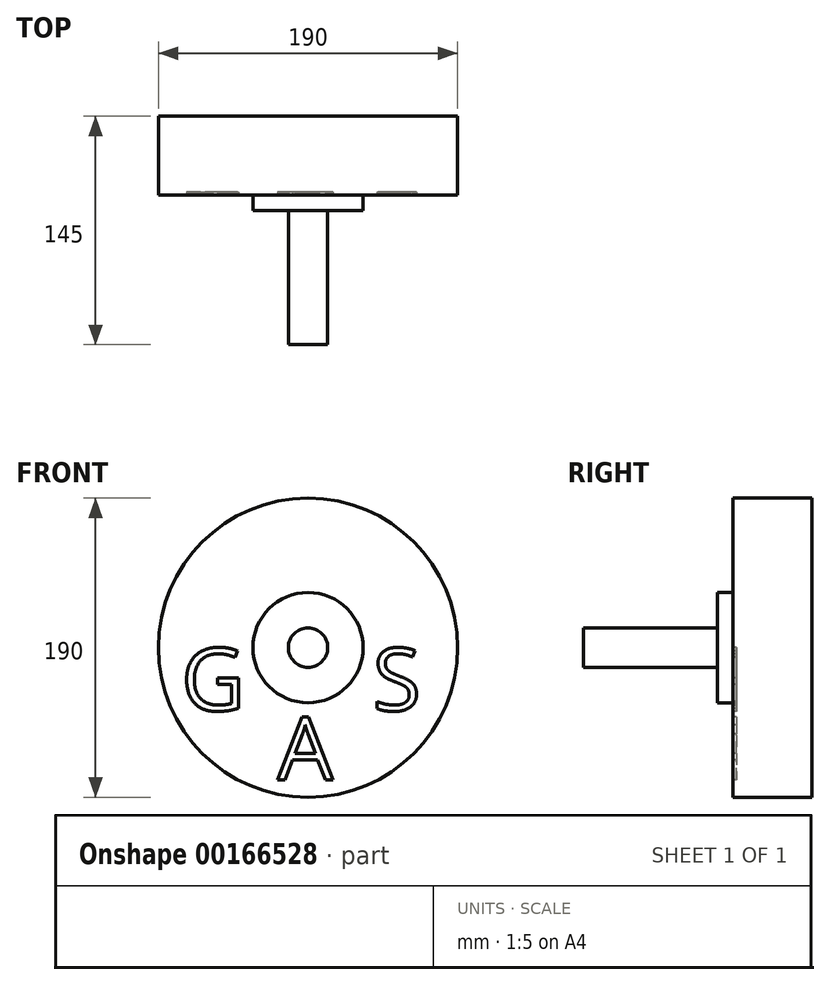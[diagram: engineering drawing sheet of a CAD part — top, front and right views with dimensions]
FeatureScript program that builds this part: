
annotation { "Feature Type Name" : "Feature", "Feature Type Description" : "" }
export const myFeature = defineFeature(function(context is Context, id is Id, definition is map)
    precondition{}
    {
        {
            var Q0;
            Q0=qCreatedBy(makeId("Front.planeOp"),FACE);
            var sketch = newSketch(context, id + "F0", { "sketchPlane" : qUnion([Q0])});
            skCircle(sketch, "E0", {"center": v(0, 0) * mm, "radius": 95 * mm});
            skCircle(sketch, "E1", {"center": v(0, 0) * mm, "radius": 35 * mm});
            skCircle(sketch, "E2", {"center": v(0, 0) * mm, "radius": 12.5 * mm});
            skSolve(sketch);
        }
        {
            var Q0;
            Q0=makeQuery(id+"F0.imprint","IMPRINT",FACE,{"disambiguationData":[TD([[makeQuery(id+"F0.imprint","IMPRINT",EDGE,{"derivedFrom":sQuery(id+"F0.wireOp",EDGE,"E2")}),1.0]])]});
            extrude(context, id + "F1", {"entities" : qUnion([Q0]), "depth" : 145 * mm});
        }
        {
            var Q0;
            Q0=makeQuery(id+"F0.imprint","IMPRINT",FACE,{"disambiguationData":[TD([[makeQuery(id+"F0.imprint","IMPRINT",EDGE,{"derivedFrom":sQuery(id+"F0.wireOp",EDGE,"E0")}),1.0]])]});
            extrude(context, id + "F2", {"entities" : qUnion([Q0]), "operationType" : NewBodyOperationType.ADD, "depth" : 50 * mm});
        }
        {
            var Q0;
            Q0=makeQuery(id+"F0.imprint","IMPRINT",FACE,{"disambiguationData":[TD([[makeQuery(id+"F0.imprint","IMPRINT",EDGE,{"derivedFrom":sQuery(id+"F0.wireOp",EDGE,"E1")}),1.0]])]});
            extrude(context, id + "F3", {"entities" : qUnion([Q0]), "operationType" : NewBodyOperationType.ADD, "depth" : 60 * mm});
        }
        {
            var Q0;
            Q0=makeQuery(id+"F2.opExtrude","CAP_FACE",FACE,{"disambiguationData":[OSD([sQuery(id+"F0.wireOp",EDGE,"E0"),sQuery(id+"F0.wireOp",EDGE,"E1")])],"isStart":false});
            var sketch = newSketch(context, id + "F4", { "sketchPlane" : qUnion([Q0])});
            skText(sketch, "E3", { "text": "G", "fontName": "OpenSans-Regular.ttf"});
            skText(sketch, "E4", { "text": "A", "fontName": "OpenSans-Regular.ttf"});
            skText(sketch, "E5", { "text": "S", "fontName": "OpenSans-Regular.ttf"});
            const initialGuessF4  = {"E3": [-0.0805, -0.04, 1, 0, 0.04], "E4": [-0.01938, -0.08396, 1, 0, 0.04], "E5": [0.04107, -0.04, 1, 0, 0.04]};
            skSetInitialGuess(sketch, initialGuessF4);
            skSolve(sketch);
        }
        {
            var Q0;
            Q0 = qSketchRegion(id + "F4", true);
            extrude(context, id + "F5", {"entities" : qUnion([Q0]), "operationType" : NewBodyOperationType.REMOVE, "oppositeDirection" : true, "depth" : 2 * mm});
        }
    });
